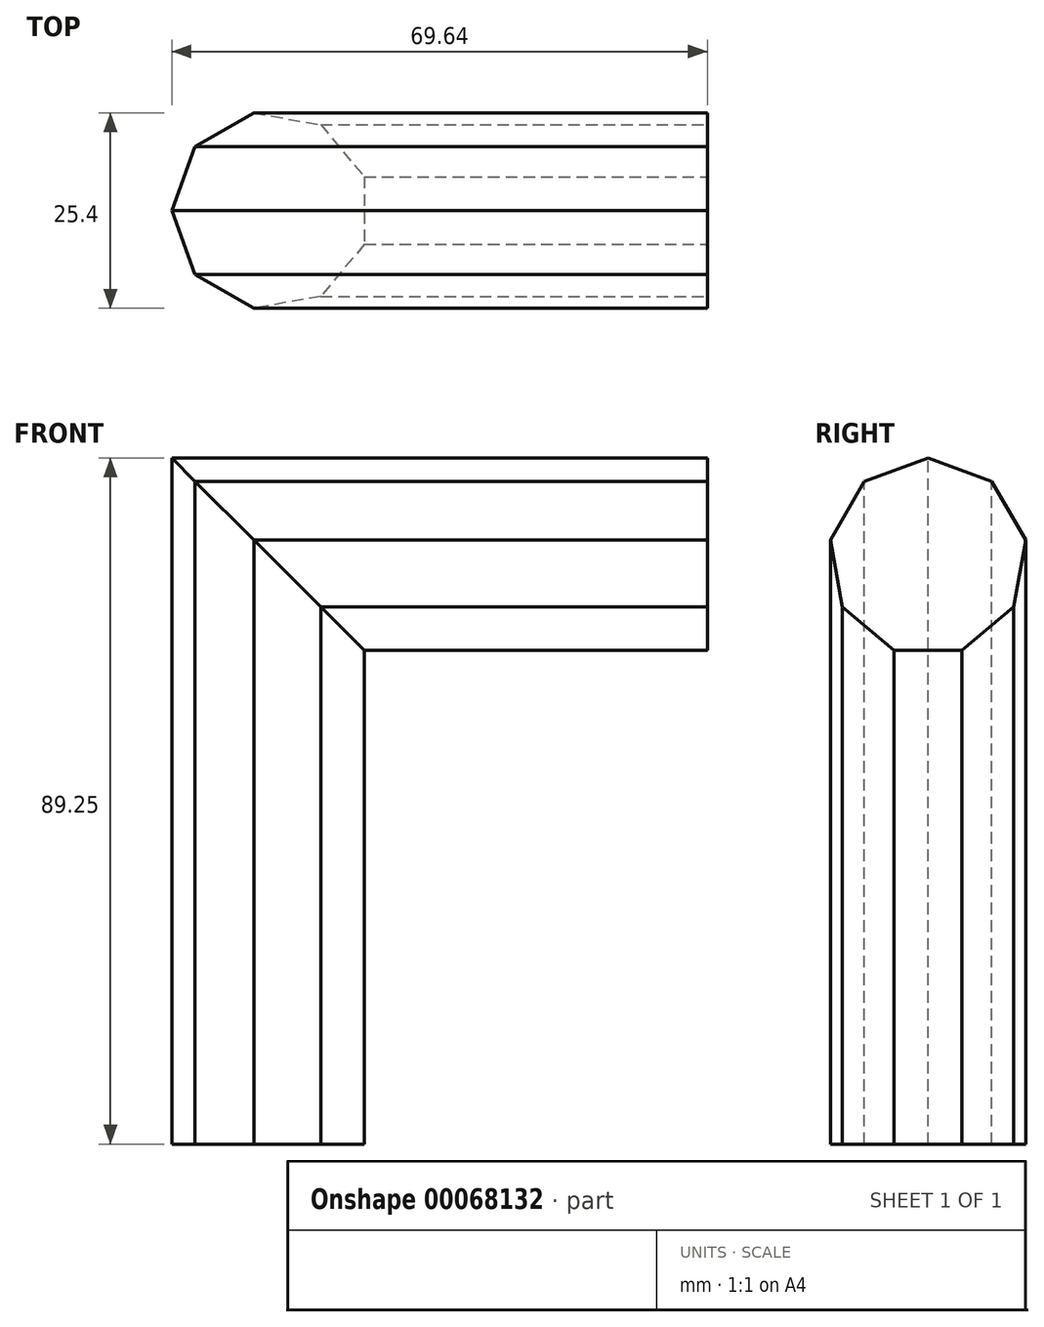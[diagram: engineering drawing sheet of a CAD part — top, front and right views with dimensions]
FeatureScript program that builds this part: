
annotation { "Feature Type Name" : "Feature", "Feature Type Description" : "" }
export const myFeature = defineFeature(function(context is Context, id is Id, definition is map)
    precondition{}
    {
        {
            var Q0;
            Q0=qCreatedBy(makeId("Top.planeOp"),FACE);
            var sketch = newSketch(context, id + "F0", { "sketchPlane" : qUnion([Q0])});
            skCircle(sketch, "E0.cCircle", {"center": v(0, 0) * mm, "radius": 12.12 * mm, "construction": true});
            skLineSegment(sketch, "E0.0", {"start": v(12.12, 4.41) * mm, "end": v(12.12, -4.41) * mm});
            skLineSegment(sketch, "E0.1", {"start": v(12.12, -4.41) * mm, "end": v(6.45, -11.17) * mm});
            skLineSegment(sketch, "E0.2", {"start": v(6.45, -11.17) * mm, "end": v(-2.24, -12.7) * mm});
            skLineSegment(sketch, "E0.3", {"start": v(-2.24, -12.7) * mm, "end": v(-9.88, -8.29) * mm});
            skLineSegment(sketch, "E0.4", {"start": v(-9.88, -8.29) * mm, "end": v(-12.9, 0) * mm});
            skLineSegment(sketch, "E0.5", {"start": v(-12.9, 0) * mm, "end": v(-9.88, 8.29) * mm});
            skLineSegment(sketch, "E0.6", {"start": v(-9.88, 8.29) * mm, "end": v(-2.24, 12.7) * mm});
            skLineSegment(sketch, "E0.7", {"start": v(-2.24, 12.7) * mm, "end": v(6.45, 11.17) * mm});
            skLineSegment(sketch, "E0.8", {"start": v(6.45, 11.17) * mm, "end": v(12.12, 4.41) * mm});
            skPoint(sketch, "E0.0.midPoint", {"position": v(12.12, 0) * mm});
            skSolve(sketch);
        }
        {
            var Q0;
            Q0=qCreatedBy(makeId("Front.planeOp"),FACE);
            var sketch = newSketch(context, id + "F1", { "sketchPlane" : qUnion([Q0])});
            skLineSegment(sketch, "E1", {"start": v(0, 0) * mm, "end": v(0, 76.35) * mm});
            skLineSegment(sketch, "E2", {"start": v(0, 76.35) * mm, "end": v(56.74, 76.35) * mm});
            skSolve(sketch);
        }
        {
            var Q0;
            Q0=makeQuery(id+"F0.imprint","IMPRINT",FACE,{"disambiguationData":[TD([[makeQuery(id+"F0.imprint","IMPRINT",EDGE,{"derivedFrom":sQuery(id+"F0.wireOp",EDGE,"E0.0")}),-1.0]])]});
            var Q1;
            Q1=sQuery(id+"F1.wireOp",EDGE,"E1");
            var Q2;
            Q2=sQuery(id+"F1.wireOp",EDGE,"E2");
            sweep(context, id + "F2", {"profiles" : qUnion([Q0]), "path" : qUnion([Q1, Q2])});
        }
    });
